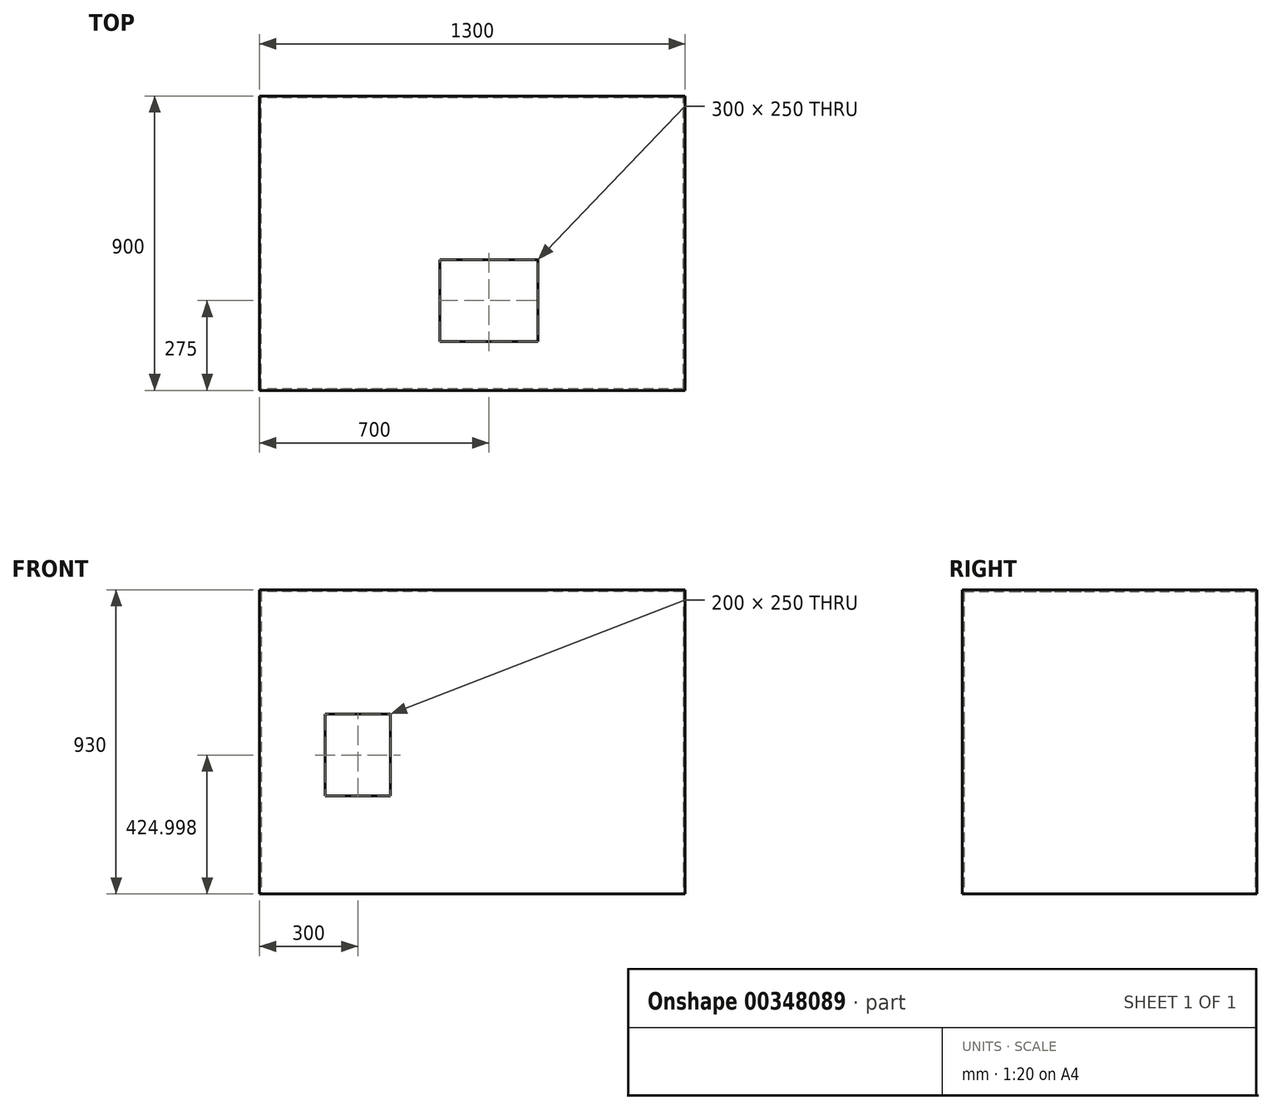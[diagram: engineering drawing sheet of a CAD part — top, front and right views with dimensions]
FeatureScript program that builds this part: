
annotation { "Feature Type Name" : "Feature", "Feature Type Description" : "" }
export const myFeature = defineFeature(function(context is Context, id is Id, definition is map)
    precondition{}
    {
        {
            var Q0;
            Q0=qCreatedBy(makeId("Front.planeOp"),FACE);
            var sketch = newSketch(context, id + "F0", { "sketchPlane" : qUnion([Q0])});
            skLineSegment(sketch, "E0.bottom", {"start": v(42.95, 877.4) * mm, "end": v(-1257.05, 877.4) * mm});
            skLineSegment(sketch, "E0.top", {"start": v(42.95, -52.6) * mm, "end": v(-1257.05, -52.6) * mm});
            skLineSegment(sketch, "E0.left", {"start": v(42.95, 877.4) * mm, "end": v(42.95, -52.6) * mm});
            skLineSegment(sketch, "E0.right", {"start": v(-1257.05, 877.4) * mm, "end": v(-1257.05, -52.6) * mm});
            skSolve(sketch);
        }
        {
            var Q0;
            Q0=makeQuery(id+"F0.imprint","IMPRINT",FACE,{"disambiguationData":[TD([[makeQuery(id+"F0.imprint","IMPRINT",EDGE,{"derivedFrom":sQuery(id+"F0.wireOp",EDGE,"E0.bottom")}),1.0]])]});
            extrude(context, id + "F1", {"entities" : qUnion([Q0]), "depth" : 900 * mm});
        }
        {
            var Q0;
            Q0=makeQuery(id+"F1.opExtrude","SWEPT_FACE",FACE,{"disambiguationData":[OSD([sQuery(id+"F0.wireOp",EDGE,"E0.top")])]});
            shell(context, id + "F2", {"entities" : qUnion([Q0]), "thickness" : 5 * mm});
        }
        {
            var Q0;
            Q0=makeQuery(id+"F1.opExtrude","CAP_FACE",FACE,{"disambiguationData":[OSD([sQuery(id+"F0.wireOp",EDGE,"E0.bottom"),sQuery(id+"F0.wireOp",EDGE,"E0.top"),sQuery(id+"F0.wireOp",EDGE,"E0.left"),sQuery(id+"F0.wireOp",EDGE,"E0.right")])],"isStart":false});
            var sketch = newSketch(context, id + "F3", { "sketchPlane" : qUnion([Q0])});
            skLineSegment(sketch, "E1.bottom", {"start": v(-1057.05, 497.4) * mm, "end": v(-857.05, 497.4) * mm});
            skLineSegment(sketch, "E1.top", {"start": v(-1057.05, 247.4) * mm, "end": v(-857.05, 247.4) * mm});
            skLineSegment(sketch, "E1.left", {"start": v(-1057.05, 497.4) * mm, "end": v(-1057.05, 247.4) * mm});
            skLineSegment(sketch, "E1.right", {"start": v(-857.05, 497.4) * mm, "end": v(-857.05, 247.4) * mm});
            skLineSegment(sketch, "E2", {"start": v(-1057.05, 247.4) * mm, "end": v(-1257.05, 247.4) * mm});
            skLineSegment(sketch, "E3", {"start": v(-1057.05, 247.4) * mm, "end": v(-1057.05, -52.6) * mm});
            skSolve(sketch);
        }
        {
            var Q0;
            Q0=makeQuery(id+"F3.imprint","IMPRINT",FACE,{"disambiguationData":[TD([[makeQuery(id+"F3.imprint","IMPRINT",EDGE,{"derivedFrom":sQuery(id+"F3.wireOp",EDGE,"E1.bottom")}),-1.0]])]});
            extrude(context, id + "F4", {"entities" : qUnion([Q0]), "operationType" : NewBodyOperationType.REMOVE, "oppositeDirection" : true, "depth" : 25 * mm});
        }
        {
            var Q0;
            Q0=makeQuery(id+"F1.opExtrude","SWEPT_FACE",FACE,{"disambiguationData":[OSD([sQuery(id+"F0.wireOp",EDGE,"E0.bottom")])]});
            var sketch = newSketch(context, id + "F5", { "sketchPlane" : qUnion([Q0])});
            skLineSegment(sketch, "E4.bottom", {"start": v(-707.05, -500) * mm, "end": v(-407.05, -500) * mm});
            skLineSegment(sketch, "E4.top", {"start": v(-707.05, -750) * mm, "end": v(-407.05, -750) * mm});
            skLineSegment(sketch, "E4.left", {"start": v(-707.05, -500) * mm, "end": v(-707.05, -750) * mm});
            skLineSegment(sketch, "E4.right", {"start": v(-407.05, -500) * mm, "end": v(-407.05, -750) * mm});
            skLineSegment(sketch, "E5", {"start": v(-407.05, -750) * mm, "end": v(-407.05, -900) * mm});
            skLineSegment(sketch, "E6", {"start": v(-707.05, -750) * mm, "end": v(-1257.05, -750) * mm});
            skSolve(sketch);
        }
        {
            var Q0;
            Q0=makeQuery(id+"F5.imprint","IMPRINT",FACE,{"disambiguationData":[TD([[makeQuery(id+"F5.imprint","IMPRINT",EDGE,{"derivedFrom":sQuery(id+"F5.wireOp",EDGE,"E4.bottom")}),-1.0]])]});
            extrude(context, id + "F6", {"entities" : qUnion([Q0]), "operationType" : NewBodyOperationType.REMOVE, "oppositeDirection" : true, "depth" : 25 * mm});
        }
    });
